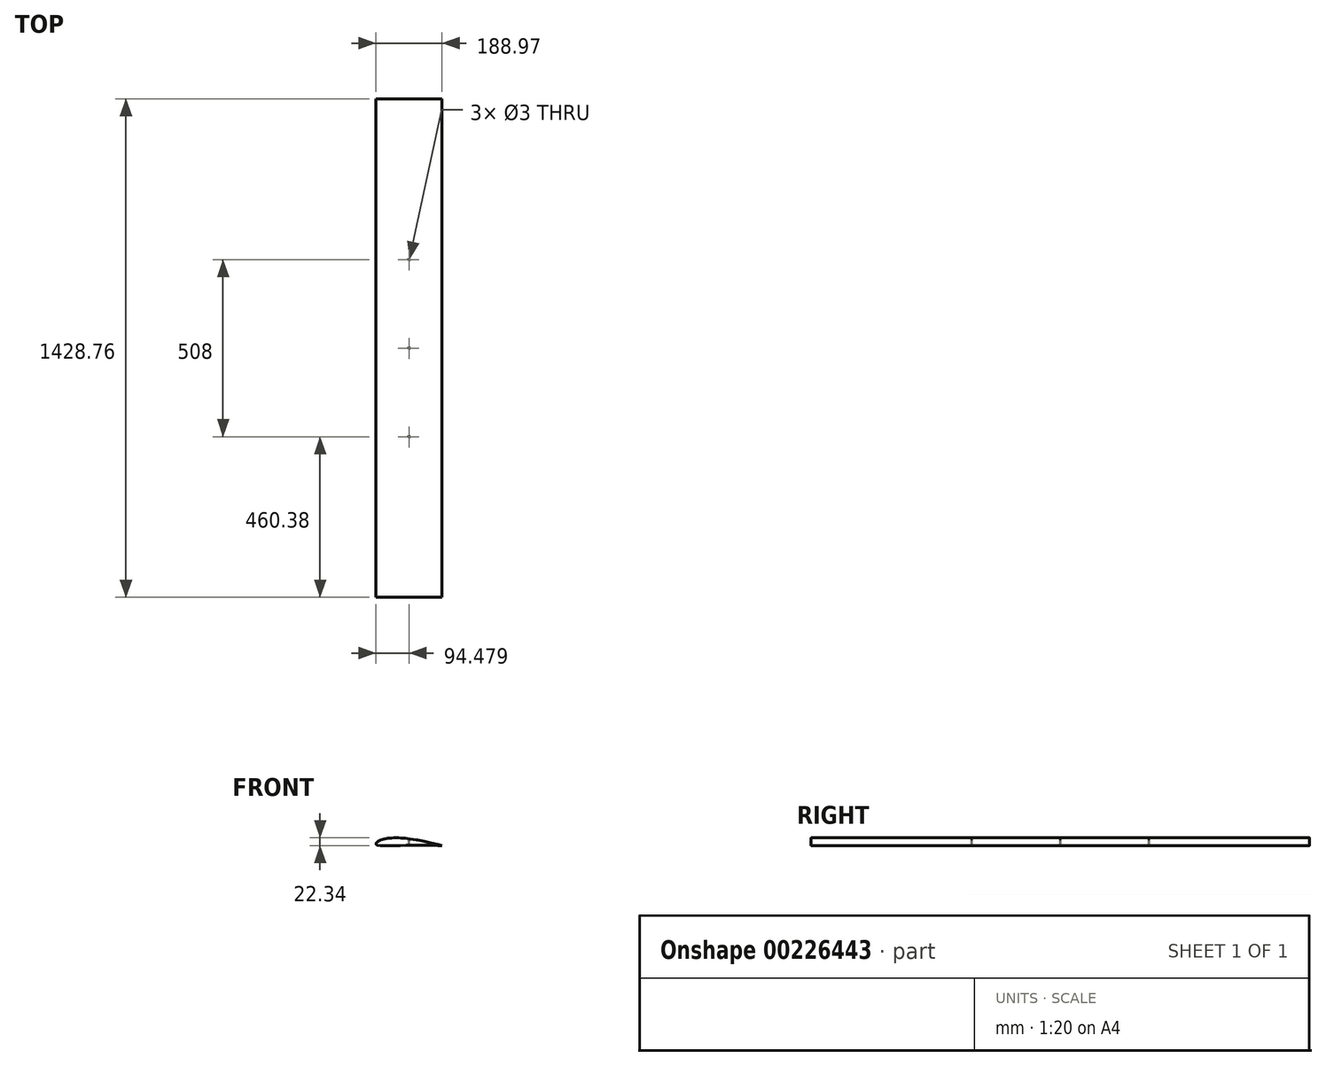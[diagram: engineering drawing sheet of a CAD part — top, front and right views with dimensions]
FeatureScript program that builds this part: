
annotation { "Feature Type Name" : "Feature", "Feature Type Description" : "" }
export const myFeature = defineFeature(function(context is Context, id is Id, definition is map)
    precondition{}
    {
        {
            var Q0;
            Q0=qCreatedBy(makeId("Front.planeOp"),FACE);
            var sketch = newSketch(context, id + "F0", { "sketchPlane" : qUnion([Q0])});
            skFitSpline(sketch, "E0.0", {"points": [v(330.51, -26.8) * mm, v(330.41, -27.02) * mm, v(320.9, -26.65) * mm, v(282.9, -25.74) * mm, v(133.46, -23.45) * mm, v(-1.4, -24.3) * mm, v(-5.52, -24.35) * mm, v(-223.27, -27.63) * mm, v(-263.84, -26.15) * mm, v(-289.63, -25.37) * mm, v(-306.1, -22.64) * mm, v(-310.34, -21.37) * mm, v(-312.97, -20.17) * mm, v(-315.36, -18.5) * mm, v(-317.44, -16.46) * mm, v(-318.92, -14.43) * mm, v(-319.94, -12.57) * mm, v(-320.57, -10.76) * mm, v(-320.82, -9.61) * mm, v(-320.99, -7.97) * mm, v(-320.86, -6.28) * mm, v(-320.4, -4.3) * mm, v(-319.53, -2.04) * mm, v(-317.5, 1.34) * mm, v(-314.64, 4.78) * mm, v(-309.38, 9.62) * mm, v(-300.92, 15.27) * mm, v(-284.86, 23.88) * mm, v(-268.85, 30.71) * mm, v(-251.3, 35.74) * mm, v(-225.1, 41.46) * mm, v(-196.52, 45.77) * mm, v(-164.68, 48.46) * mm, v(-128.36, 49.34) * mm, v(-84.95, 48.6) * mm, v(-42.8, 45.45) * mm, v(0.59, 40.3) * mm, v(69.38, 29.76) * mm, v(139.47, 17.63) * mm, v(201.78, 4.38) * mm, v(277.63, -13.26) * mm, v(320.71, -24.55) * mm, v(330.61, -26.58) * mm, v(330.51, -26.8) * mm]});
            skPoint(sketch, "E1", {"position": v(330.51, -26.8) * mm});
            skPoint(sketch, "E2", {"position": v(-320.85, -9.19) * mm});
            skSolve(sketch);
        }
        {
            var Q0;
            Q0=makeQuery(id+"F0.imprint","IMPRINT",FACE,{"disambiguationData":[TD([[makeQuery(id+"F0.imprint","IMPRINT",EDGE,{"derivedFrom":sQuery(id+"F0.wireOp",EDGE,"E0.0")}),-1.0]])]});
            extrude(context, id + "F1", {"entities" : qUnion([Q0]), "depth" : 635 * mm, "offsetDistance" : 25.4 * mm, "symmetric" : true});
        }
        {
            var Q0;
            Q0=makeQuery(id+"F1.opExtrude","SWEPT_BODY",BODY,{"disambiguationData":[OSD([sQuery(id+"F0.wireOp",EDGE,"E0.0")])]});
            var Q1;
            Q1=qCreatedBy(makeId("Origin.pointOp"),VERTEX);
            transform(context, id + "F2", {"entities" : qUnion([Q0]), "transformType" : TransformType.SCALE_UNIFORMLY, "scale" : .29, "scalePoint" : qUnion([Q1]), "makeCopy" : false});
        }
        {
            var Q0;
            Q0=makeQuery(id+"F1.opExtrude","CAP_FACE",FACE,{"disambiguationData":[OSD([sQuery(id+"F0.wireOp",EDGE,"E0.0")])],"isStart":false});
            var sketch = newSketch(context, id + "F3", { "sketchPlane" : qUnion([Q0])});
            skFitSpline(sketch, "E3.0", {"points": [v(95.85, -7.77) * mm, v(95.82, -7.84) * mm, v(93.06, -7.73) * mm, v(82.04, -7.47) * mm, v(38.7, -6.8) * mm, v(-0.4, -7.05) * mm, v(-1.6, -7.06) * mm, v(-64.75, -8.01) * mm, v(-76.51, -7.58) * mm, v(-84, -7.36) * mm, v(-88.77, -6.57) * mm, v(-90, -6.2) * mm, v(-90.76, -5.85) * mm, v(-91.45, -5.37) * mm, v(-92.06, -4.77) * mm, v(-92.49, -4.19) * mm, v(-92.78, -3.65) * mm, v(-92.96, -3.12) * mm, v(-93.04, -2.79) * mm, v(-93.09, -2.31) * mm, v(-93.05, -1.82) * mm, v(-92.92, -1.25) * mm, v(-92.66, -0.6) * mm, v(-92.08, 0.39) * mm, v(-91.24, 1.39) * mm, v(-89.72, 2.79) * mm, v(-87.27, 4.43) * mm, v(-82.61, 6.93) * mm, v(-77.97, 8.9) * mm, v(-72.88, 10.37) * mm, v(-65.28, 12.02) * mm, v(-57, 13.27) * mm, v(-47.76, 14.05) * mm, v(-37.23, 14.3) * mm, v(-24.64, 14.1) * mm, v(-12.41, 13.18) * mm, v(0.17, 11.69) * mm, v(20.12, 8.63) * mm, v(40.45, 5.11) * mm, v(58.52, 1.27) * mm, v(80.51, -3.84) * mm, v(93, -7.12) * mm, v(95.88, -7.7) * mm, v(95.85, -7.77) * mm]});
            skCircle(sketch, "E4", {"center": v(-69.03, 1.21) * mm, "radius": 0.64 * mm});
            skCircle(sketch, "E5", {"center": v(-17.85, 2.7) * mm, "radius": 0.64 * mm});
            skCircle(sketch, "E6", {"center": v(50.28, -1.1) * mm, "radius": 0.64 * mm});
            skSolve(sketch);
        }
        {
            var Q0;
            Q0=makeQuery(id+"F1.opExtrude","CAP_FACE",FACE,{"disambiguationData":[OSD([sQuery(id+"F0.wireOp",EDGE,"E0.0")])],"isStart":true});
            extrude(context, id + "F4", {"entities" : qUnion([Q0]), "operationType" : NewBodyOperationType.ADD, "depth" : 1244.6 * mm, "offsetDistance" : 25.4 * mm});
        }
        {
            var Q0;
            Q0=qCreatedBy(makeId("Top.planeOp"),FACE);
            var sketch = newSketch(context, id + "F5", { "sketchPlane" : qUnion([Q0])});
            skPoint(sketch, "E7.0", {"position": v(-17.85, -92.08) * mm});
            skLineSegment(sketch, "E8", {"start": v(-17.85, -92.08) * mm, "end": v(-17.85, 1336.67) * mm});
            skPoint(sketch, "E9", {"position": v(-17.85, 622.3) * mm});
            skLineSegment(sketch, "E10", {"start": v(1.39, 368.3) * mm, "end": v(1.39, 622.3) * mm});
            skLineSegment(sketch, "E11", {"start": v(1.39, 622.3) * mm, "end": v(1.39, 876.3) * mm});
            skLineSegment(sketch, "E12.0", {"start": v(95.85, -92.08) * mm, "end": v(-93.07, -92.08) * mm});
            skPoint(sketch, "E13", {"position": v(1.39, -92.08) * mm});
            skCircle(sketch, "E14", {"center": v(1.39, 368.3) * mm, "radius": 1.5 * mm});
            skCircle(sketch, "E15", {"center": v(1.39, 622.3) * mm, "radius": 1.5 * mm});
            skCircle(sketch, "E16", {"center": v(1.39, 876.3) * mm, "radius": 1.5 * mm});
            skSolve(sketch);
        }
        {
            var Q0;
            Q0 = qSketchRegion(id + "F5", true);
            extrude(context, id + "F6", {"entities" : qUnion([Q0]), "operationType" : NewBodyOperationType.REMOVE, "oppositeDirection" : true, "depth" : 76.2 * mm, "offsetDistance" : 25.4 * mm, "symmetric" : true});
        }
    });
